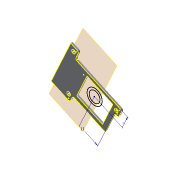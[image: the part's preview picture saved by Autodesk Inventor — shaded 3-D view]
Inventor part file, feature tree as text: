
AUTODESK INVENTOR PART (.ipt)
format: ipt  version: 2019 (Build 230136000, 136)  size: 132,608 bytes
history: native  units: mm
features: other x3, plane x1, extrude x1, fillet x1, sketch x1
ambient origin geometry x8: Origin, YZ Plane, XZ Plane, XY Plane, X Axis, Y Axis, Z Axis, Center Point
bodies: Solid1 (feature_tree)
feature tree (7):
  plane  "Work Plane1"
  extrude  "Extrusion1"  Depth=2.0mm
  fillet  "Fillet1"  Radius=2.0mm
  sketch  "Sketch1"  dims[d0=2.0mm d1=2.0mm d2=2.0mm d3=28.0mm d5=15.5mm d6=5.0mm d8=20.5mm d9=2.5mm d10=1.0mm d12=3.0mm d13=33.0mm d14=25.7mm d15=17.1mm d16=1.0mm d17=0.0mm d18=1.0mm d23=30.5mm d24=9.0mm d25=2.5mm]
  other  "Assembly_cube_StormChip_v4.iam"
  other  "Assembly_Lens_Thorlabs_Mount_KES400_Bluraylasermount:1"
  other  "20_Adapter_Bluray_KES400_Lens_Thorlabs:1"
